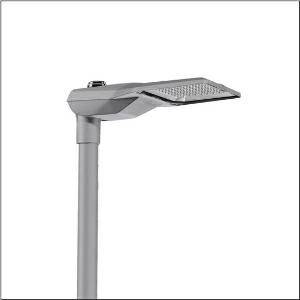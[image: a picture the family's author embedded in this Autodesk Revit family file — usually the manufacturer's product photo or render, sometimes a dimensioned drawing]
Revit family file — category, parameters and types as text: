
# Revit family: streetlight_sl_21_midi___stw1_0a_5xe7e37n08mb_6d50
name_source: partatom
category: Lighting Fixtures
units: mm (PartAtom-declared; Revit-internal decimal feet)

## family parameters
Cut with Voids When Loaded = No
Host = Face
Light Source = No
Part Type = Normal
Room Calculation Point = No
Round Connector Dimension = Use Diameter
Shared = No

## types (1)
- --- (1 x LED, 18270 lm, 136 W, 3000K)
    Apparent Load = 136 VA
    CIE Flux Codes = 38 75 98 100 100
    Color Rendering = 70
    Color Temperature = 3000K
    Default Elevation = 1800 mm
    Description = Streetlight SL 21 midi, mast luminaire, primary light control with lens, of PMMA, primary optical cover: cover, of toughened safety glass, transparent, light distribution: STW1.0a, light emission: direct distribution, primary light characteristic: asymmetric, installation type: side-entry, LED, 3G 2.5mm², High Power LED, rated luminous flux: 18.270lm, luminous efficacy: 134lm/W, light colour: 730, colour temperature: 3000K, control: overheat protection, presetting dimming linear, constant luminous flux control, time-dependent luminous flux control, flexible luminous flux parameterisation, mains connection: 220..240V, AC, 50/60Hz, connection cable pre-assembled, cable length: 12,5m, wiring characteristics: H05VV-F, start of lifetime: 136W, end of service life: 142W, reduction: 61W, luminaire housing, of diecast aluminium (EN AC-44300), powder-coated, Siteco® metallic grey (DB 702S), corrosivity category C5 mid according to DIN EN ISO 12944, multi-level sealing system, sealing non-destructively replaceable, inclination adjustable: 0°, 5°, 10°, 15°, length: 644mm, width: 335mm, height: 110mm, spigot size: 42mm (side-entry), protection rating (complete): IP66, insulation class (complete): insulation class I (protective earthing), certification: CE, ENEC, ENEC+, VDE, impact resistance: IK09, permissible operating ambient temperature for outdoor applications: -40..+50°C, standard-compliant lighting for roads and squares, packaging unit: 1 piece

Light Distribution: STW1.0a
    Height = 111 mm
    Lamp = 1 x LED
    Lamp Light Flux = 18270 lm
    Lamp Power = 136 W
    Lamp count = 1
    Length = 644 mm
    Luminous efficacy = 134 lm/W
    Manufacturer = Siteco
    ModVariant = No
    Model = 5XE7E37N08MB
    Number of Poles = 1
    OnlyDefault = Yes
    Power Factor = 1
    Product Name = Streetlight SL 21 midi | STW1.0a
    Product group = mast luminaire | pylon top
    ProductGroupID = 6100
    Protection Class = Protection class I
    Protection Degree = IP 66
    RLX_Detail_Level = 1
    RLX_Emergency_Light_Flux = 0 lm
    RLX_Emergency_Type = 0
    RLX_Emergency_Type_DB = No
    RlxData = <blob elided: 90501 chars, md5=b8f832d9>
    Socket = socket
    Standby Power = 0 W
    System Light Flux = 18270 lm
    System Power = 136 W
    Type Comments = factory setting: luminous flux: 100 % | dim-lin: 254 | 695 mA
    Type Image = l_1294377.jpg
    URL = http://relux.com
    VarID = @adj_084897
    Voltage = 0 V
    Weight = 0.00 kg
    Width = 336 mm

## geometry (parser evidence)
native form markers: Blend x4, Sweep x10
no freeform markers — native parametric forms only
